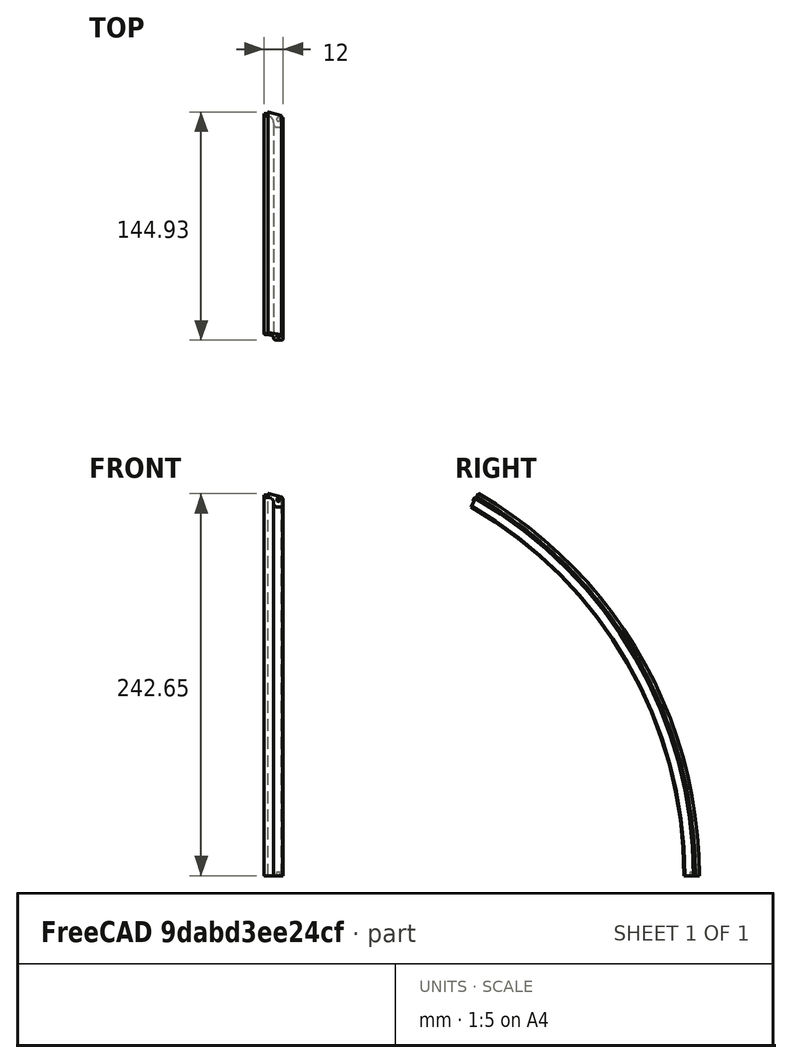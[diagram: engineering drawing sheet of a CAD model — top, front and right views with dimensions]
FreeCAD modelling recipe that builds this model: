
FCSTD DOCUMENT  (FreeCAD 0.16R)
Label: BeadLock4
License: All rights reserved
LicenseURL: http://en.wikipedia.org/wiki/All_rights_reserved
objects: PartDesign::Fillet×5, Sketcher::SketchObject×3, PartDesign::Chamfer×2, PartDesign::Revolution×1, PartDesign::Pad×1, PartDesign::Pocket×1, Mesh::Feature×1
note: 16 computed .brp shape members not serialized (recipe doc carries the construction recipe); baked Part::Feature solids carry a one-line shape summary decoded from their .brp

FEATURE [Sketcher::SketchObject] Sketch
  sketch-geometry (8):
    g0: LineSegment StartX=0 StartY=279 StartZ=0 EndX=2.5 EndY=279 EndZ=0
    g1: LineSegment StartX=2.5 StartY=279 StartZ=0 EndX=2.5 EndY=280.25 EndZ=0
    g2: LineSegment StartX=0 StartY=277.5 StartZ=0 EndX=0 EndY=279 EndZ=0
    g3: LineSegment StartX=0 StartY=277.5 StartZ=0 EndX=6 EndY=277.5 EndZ=0
    g4: LineSegment StartX=6 StartY=277.5 StartZ=0 EndX=6 EndY=270.5 EndZ=0
    g5: LineSegment StartX=6 StartY=270.5 StartZ=0 EndX=12 EndY=270.5 EndZ=0
    g6: LineSegment StartX=12 StartY=270.5 StartZ=0 EndX=12 EndY=277.5 EndZ=0
    g7: LineSegment StartX=2.5 StartY=280.25 StartZ=0 EndX=12 EndY=277.5 EndZ=0
  constraints (24):
    c: Horizontal(g0)
    c: PointOnObject(g0,g-2)
    c: DistanceY(g0) = 279
    c: Distance(g0) = 2.5
    c: Coincident(g1,g0)
    c: Vertical(g1)
    c: Distance(g1) = 1.25
    c: Vertical(g2)
    c: Coincident(g2,g0)
    c: Distance(g2) = 1.5
    c: Horizontal(g3)
    c: Coincident(g3,g2)
    c: Distance(g3) = 6
    c: Vertical(g4)
    c: Coincident(g4,g3)
    c: Distance(g4) = 7
    c: Horizontal(g5)
    c: Coincident(g5,g4)
    c: Distance(g5) = 6
    c: Vertical(g6)
    c: Coincident(g5,g6)
    c: Distance(g6) = 7
    c: Coincident(g7,g1)
    c: Coincident(g7,g6)
FEATURE [PartDesign::Revolution] Revolution
  Angle = 60
  Axis = (1,0,0)
  Base = (0,0,0)
  ReferenceAxis = -> Sketch [H_Axis]
  Sketch = -> Sketch
FEATURE [PartDesign::Fillet] Fillet
  Base = -> Revolution [Edge17]
  Radius = 4
FEATURE [PartDesign::Fillet] Fillet001
  Base = -> Fillet [Edge23]
  Radius = 1
FEATURE [PartDesign::Fillet] Fillet002
  Base = -> Fillet001 [Edge22]
  Radius = 0.4
FEATURE [PartDesign::Fillet] Fillet003
  Base = -> Fillet002 [Edge19]
  Radius = 0.2
FEATURE [PartDesign::Chamfer] Chamfer
  Base = -> Fillet003 [Edge20]
  Size = 1
FEATURE [PartDesign::Chamfer] Chamfer001
  Base = -> Chamfer [Edge21]
  Size = 0.5
FEATURE [PartDesign::Fillet] Fillet004
  Base = -> Chamfer001 [Edge22]
  Radius = 2
FEATURE [Sketcher::SketchObject] Sketch001
  ExternalGeometry = -> [Fillet004]
  Placement = pos=(0,0,0) rot=(1,0,0;1.0472rad)
  Support = -> Fillet004 [Face17]
  sketch-geometry (1):
    g0: Circle CenterX=9 CenterY=275.5 CenterZ=0 NormalX=0 NormalY=0 NormalZ=1 Radius=1
  constraints (4):
    c: Radius(g0) = 1
    c: Distance(g0,g-3) = 3
    c: DistanceY(g-3) = 276.5
    c: Distance(g0,g-4) = 5
FEATURE [PartDesign::Pad] Pad
  Length = 1
  Length2 = 100
  Sketch = -> Sketch001
  Type = 0
FEATURE [Sketcher::SketchObject] Sketch002
  ExternalGeometry = -> [Pad]
  Placement = pos=(0,0,0) rot=(1,0,0;3.14159rad)
  Support = -> Pad [Face19]
  sketch-geometry (1):
    g0: Circle CenterX=9 CenterY=-275.5 CenterZ=0 NormalX=0 NormalY=0 NormalZ=1 Radius=1.1
  constraints (3):
    c: Radius(g0) = 1.1
    c: Distance(g0,g-4) = 5
    c: Distance(g0,g-3) = 3
FEATURE [PartDesign::Pocket] Pocket
  Length = 2
  Sketch = -> Sketch002
  Type = 0
FEATURE [Mesh::Feature] Mesh  label="Pocket (Meshed)"
